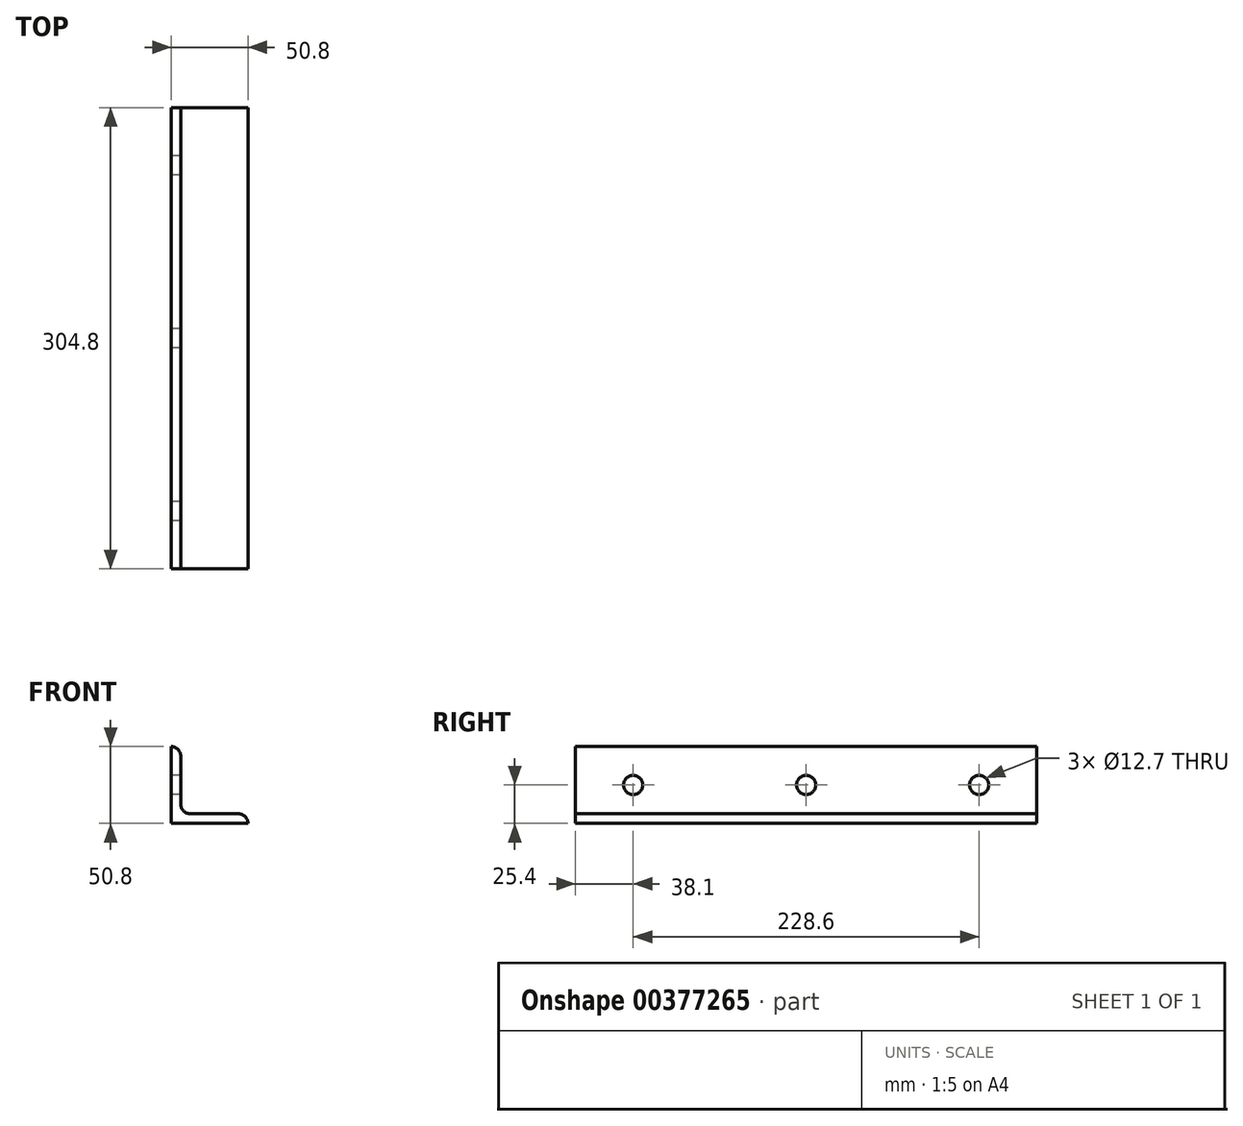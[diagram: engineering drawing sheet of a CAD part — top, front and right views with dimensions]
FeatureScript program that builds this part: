
annotation { "Feature Type Name" : "Feature", "Feature Type Description" : "" }
export const myFeature = defineFeature(function(context is Context, id is Id, definition is map)
    precondition{}
    {
        {
            var Q0;
            Q0=qCreatedBy(makeId("Front.planeOp"),FACE);
            var sketch = newSketch(context, id + "F0", { "sketchPlane" : qUnion([Q0])});
            skLineSegment(sketch, "E0.bottom", {"start": v(0, 0) * mm, "end": v(50.8, 0) * mm});
            skLineSegment(sketch, "E1", {"start": v(0, 0) * mm, "end": v(0, 50.8) * mm});
            skLineSegment(sketch, "E2", {"start": v(0, 50.8) * mm, "end": v(0, 50.8) * mm});
            skLineSegment(sketch, "E3", {"start": v(6.35, 44.45) * mm, "end": v(6.35, 12.7) * mm});
            skLineSegment(sketch, "E4", {"start": v(12.7, 6.35) * mm, "end": v(44.45, 6.35) * mm});
            skLineSegment(sketch, "E5", {"start": v(50.8, 0) * mm, "end": v(50.8, 0) * mm});
            skPoint(sketch, "E6.visualSharp", {"position": v(6.35, 50.8) * mm});
            skArc(sketch, "E6.filletArc", {"start": v(6.35, 44.45) * mm, "mid": v(4.5, 48.94) * mm, "end": v(0, 50.8) * mm});
            skPoint(sketch, "E7.visualSharp", {"position": v(50.8, 6.35) * mm});
            skArc(sketch, "E7.filletArc", {"start": v(50.8, 0) * mm, "mid": v(48.94, 4.5) * mm, "end": v(44.45, 6.35) * mm});
            skPoint(sketch, "E8.visualSharp", {"position": v(6.35, 6.35) * mm});
            skArc(sketch, "E8.filletArc", {"start": v(6.35, 12.7) * mm, "mid": v(8.2, 8.2) * mm, "end": v(12.7, 6.35) * mm});
            skSolve(sketch);
        }
        {
            var Q0;
            Q0 = qSketchRegion(id + "F0", true);
            extrude(context, id + "F1", {"entities" : qUnion([Q0]), "oppositeDirection" : true, "depth" : 304.8 * mm});
        }
        {
            var Q0;
            Q0=makeQuery(id+"F1.opExtrude","SWEPT_FACE",FACE,{"disambiguationData":[OSD([sQuery(id+"F0.wireOp",EDGE,"E1")])]});
            var sketch = newSketch(context, id + "F2", { "sketchPlane" : qUnion([Q0])});
            skLineSegment(sketch, "E9", {"start": v(0, 25.4) * mm, "end": v(-38.1, 25.4) * mm, "construction": true});
            skCircle(sketch, "E10", {"center": v(-38.1, 25.4) * mm, "radius": 6.35 * mm});
            skSolve(sketch);
        }
        {
            var Q0;
            Q0=makeQuery(id+"F2.imprint","IMPRINT",FACE,{"disambiguationData":[TD([[makeQuery(id+"F2.imprint","IMPRINT",EDGE,{"derivedFrom":sQuery(id+"F2.wireOp",EDGE,"E10")}),1.0]])]});
            extrude(context, id + "F3", {"entities" : qUnion([Q0]), "operationType" : NewBodyOperationType.REMOVE, "oppositeDirection" : true, "depth" : 6.35 * mm});
        }
        {
            var Q0;
            Q0=makeQuery(id+"F1.opExtrude","SWEPT_FACE",FACE,{"disambiguationData":[OSD([sQuery(id+"F0.wireOp",EDGE,"E1")])]});
            var sketch = newSketch(context, id + "F4", { "sketchPlane" : qUnion([Q0])});
            skLineSegment(sketch, "E11", {"start": v(-304.8, 25.4) * mm, "end": v(-266.7, 25.4) * mm, "construction": true});
            skCircle(sketch, "E12", {"center": v(-266.7, 25.4) * mm, "radius": 6.35 * mm});
            skSolve(sketch);
        }
        {
            var Q0;
            Q0=makeQuery(id+"F4.imprint","IMPRINT",FACE,{"disambiguationData":[TD([[makeQuery(id+"F4.imprint","IMPRINT",EDGE,{"derivedFrom":sQuery(id+"F4.wireOp",EDGE,"E12")}),1.0]])]});
            extrude(context, id + "F5", {"entities" : qUnion([Q0]), "operationType" : NewBodyOperationType.REMOVE, "oppositeDirection" : true, "depth" : 6.35 * mm});
        }
        {
            var Q0;
            Q0=makeQuery(id+"F1.opExtrude","SWEPT_FACE",FACE,{"disambiguationData":[OSD([sQuery(id+"F0.wireOp",EDGE,"E1")])]});
            var sketch = newSketch(context, id + "F6", { "sketchPlane" : qUnion([Q0])});
            skLineSegment(sketch, "E13", {"start": v(-304.8, 25.4) * mm, "end": v(0, 25.4) * mm, "construction": true});
            skLineSegment(sketch, "E14", {"start": v(-152.4, 50.8) * mm, "end": v(-152.4, 0) * mm, "construction": true});
            skCircle(sketch, "E15", {"center": v(-152.4, 25.4) * mm, "radius": 6.35 * mm});
            skSolve(sketch);
        }
        {
            var Q0;
            Q0=makeQuery(id+"F6.imprint","IMPRINT",FACE,{"disambiguationData":[TD([[makeQuery(id+"F6.imprint","IMPRINT",EDGE,{"derivedFrom":sQuery(id+"F6.wireOp",EDGE,"E15")}),1.0]])]});
            extrude(context, id + "F7", {"entities" : qUnion([Q0]), "operationType" : NewBodyOperationType.REMOVE, "oppositeDirection" : true, "depth" : 6.35 * mm});
        }
    });
